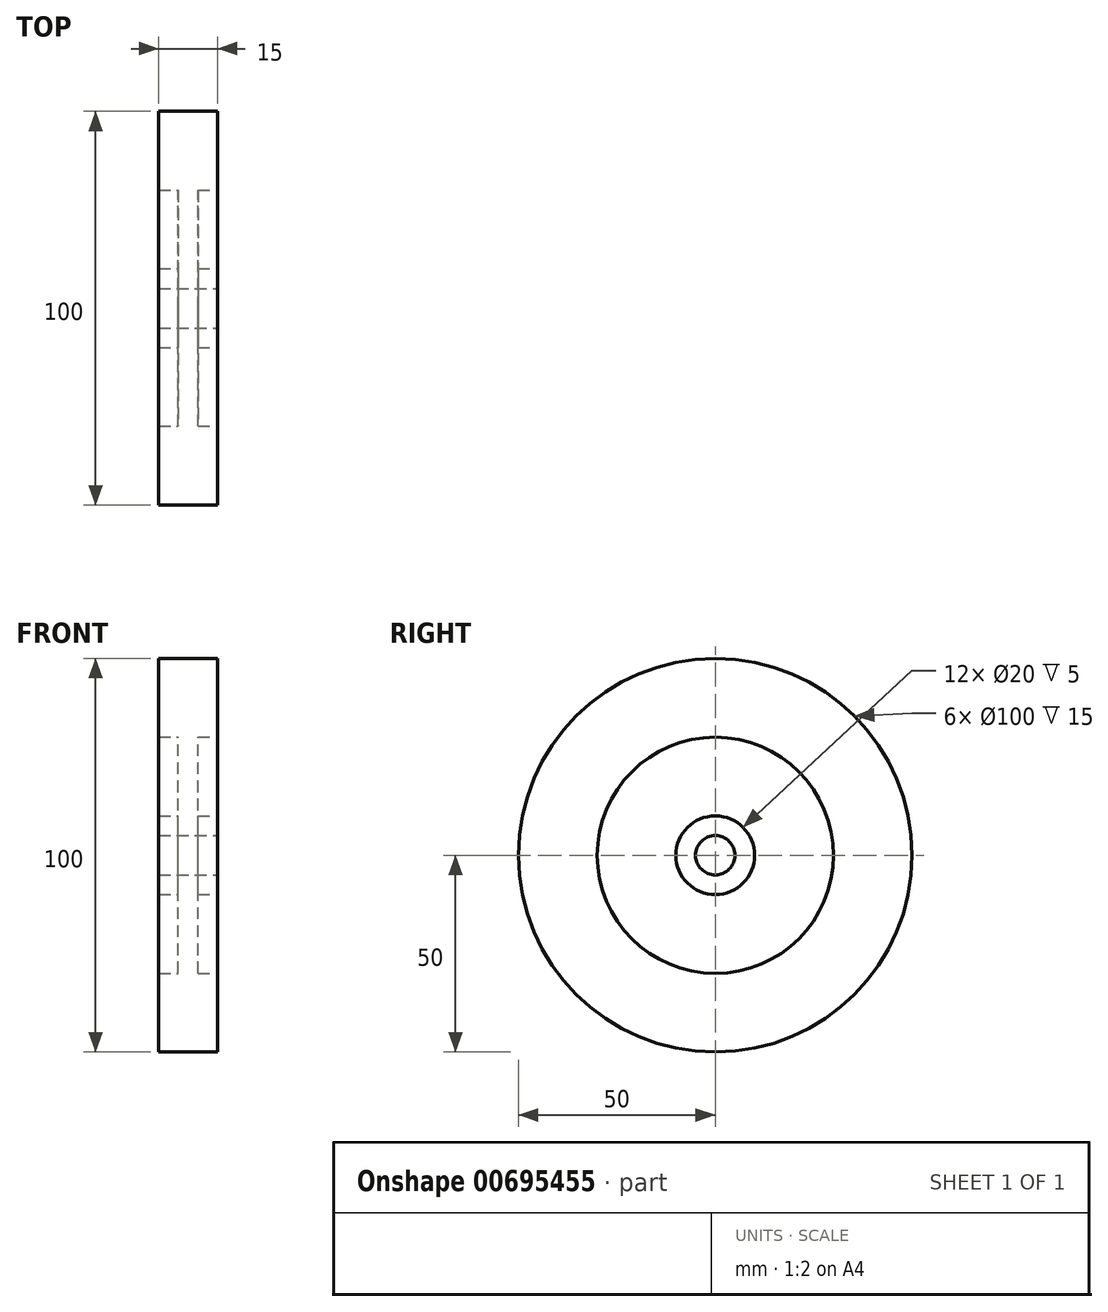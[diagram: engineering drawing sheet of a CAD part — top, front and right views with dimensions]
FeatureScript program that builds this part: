
annotation { "Feature Type Name" : "Feature", "Feature Type Description" : "" }
export const myFeature = defineFeature(function(context is Context, id is Id, definition is map)
    precondition{}
    {
        {
            var Q0;
            Q0=qCreatedBy(makeId("Front.planeOp"),FACE);
            var sketch = newSketch(context, id + "F0", { "sketchPlane" : qUnion([Q0])});
            skLineSegment(sketch, "E0", {"start": v(-7.5, 50) * mm, "end": v(7.5, 50) * mm});
            skLineSegment(sketch, "E1", {"start": v(7.5, 50) * mm, "end": v(7.5, 30) * mm});
            skLineSegment(sketch, "E2", {"start": v(7.5, 30) * mm, "end": v(2.5, 30) * mm});
            skLineSegment(sketch, "E3", {"start": v(2.5, 30) * mm, "end": v(2.5, 10) * mm});
            skLineSegment(sketch, "E4", {"start": v(2.5, 10) * mm, "end": v(7.5, 10) * mm});
            skLineSegment(sketch, "E5", {"start": v(7.5, 10) * mm, "end": v(7.5, 5) * mm});
            skLineSegment(sketch, "E6", {"start": v(7.5, 5) * mm, "end": v(-7.5, 5) * mm});
            skLineSegment(sketch, "E7", {"start": v(-7.5, 5) * mm, "end": v(-7.5, 10) * mm});
            skLineSegment(sketch, "E8", {"start": v(-7.5, 10) * mm, "end": v(-2.5, 10) * mm});
            skLineSegment(sketch, "E9", {"start": v(-2.5, 10) * mm, "end": v(-2.5, 30) * mm});
            skLineSegment(sketch, "E10", {"start": v(-2.5, 30) * mm, "end": v(-7.5, 30) * mm});
            skLineSegment(sketch, "E11", {"start": v(-7.5, 30) * mm, "end": v(-7.5, 50) * mm});
            skSolve(sketch);
        }
        {
            var Q0;
            Q0=qCreatedBy(makeId("Front.planeOp"),FACE);
            var sketch = newSketch(context, id + "F1", { "sketchPlane" : qUnion([Q0])});
            skLineSegment(sketch, "E12", {"start": v(-34.81, 0) * mm, "end": v(43.5, 0) * mm, "construction": true});
            skSolve(sketch);
        }
        {
            var Q0;
            Q0=sQuery(id+"F1.wireOp",EDGE,"E12");
            var Q1;
            Q1=sQuery(id+"F0.wireOp",EDGE,"E8");
            var Q2;
            Q2=sQuery(id+"F0.wireOp",EDGE,"E6");
            var Q3;
            Q3=sQuery(id+"F0.wireOp",EDGE,"E4");
            var Q4;
            Q4=sQuery(id+"F0.wireOp",EDGE,"E7");
            var Q5;
            Q5=sQuery(id+"F0.wireOp",EDGE,"E3");
            var Q6;
            Q6=sQuery(id+"F0.wireOp",EDGE,"E9");
            var Q7;
            Q7=sQuery(id+"F0.wireOp",EDGE,"E5");
            var Q8;
            Q8=sQuery(id+"F0.wireOp",EDGE,"E10");
            var Q9;
            Q9=sQuery(id+"F0.wireOp",EDGE,"E2");
            var Q10;
            Q10=sQuery(id+"F0.wireOp",EDGE,"E11");
            var Q11;
            Q11=sQuery(id+"F0.wireOp",EDGE,"E1");
            var Q12;
            Q12=sQuery(id+"F0.wireOp",EDGE,"E0");
            var Q13;
            Q13=sQuery(id+"F1.wireOp",EDGE,"E12");
            revolve(context, id + "F2", {"bodyType" : ToolBodyType.SURFACE, "surfaceOperationType" : NewSurfaceOperationType.NEW, "surfaceEntities" : qUnion([Q0, Q1, Q2, Q3, Q4, Q5, Q6, Q7, Q8, Q9, Q10, Q11, Q12]), "axis" : qUnion([Q13]), "revolveType" : RevolveType.FULL});
        }
    });
